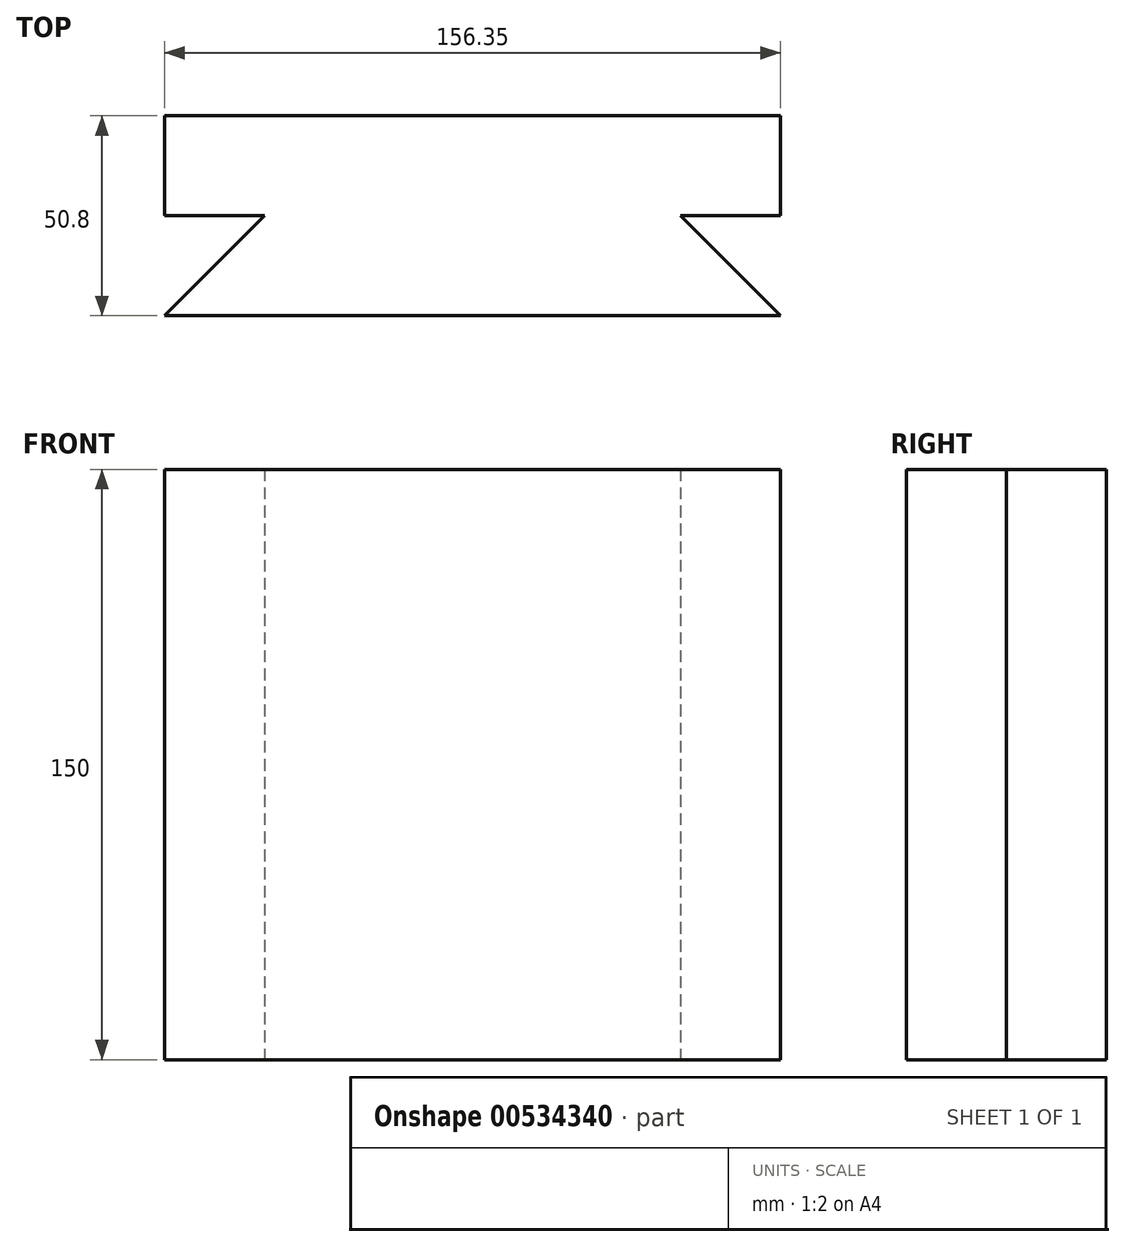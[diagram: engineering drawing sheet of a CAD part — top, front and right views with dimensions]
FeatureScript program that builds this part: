
annotation { "Feature Type Name" : "Feature", "Feature Type Description" : "" }
export const myFeature = defineFeature(function(context is Context, id is Id, definition is map)
    precondition{}
    {
        {
            var Q0;
            Q0=qCreatedBy(makeId("Top.planeOp"),FACE);
            var sketch = newSketch(context, id + "F0", { "sketchPlane" : qUnion([Q0])});
            skLineSegment(sketch, "E0.bottom", {"start": v(-77.43, 55.7) * mm, "end": v(78.92, 55.7) * mm});
            skLineSegment(sketch, "E0.top", {"start": v(-77.43, 30.3) * mm, "end": v(-52.03, 30.3) * mm});
            skLineSegment(sketch, "E0.left", {"start": v(-77.43, 55.7) * mm, "end": v(-77.43, 30.3) * mm});
            skLineSegment(sketch, "E0.right", {"start": v(78.92, 55.7) * mm, "end": v(78.92, 30.3) * mm});
            skLineSegment(sketch, "E1", {"start": v(-52.03, 30.3) * mm, "end": v(-52.03, 4.9) * mm, "construction": true});
            skLineSegment(sketch, "E2", {"start": v(53.52, 30.3) * mm, "end": v(53.52, 4.9) * mm, "construction": true});
            skLineSegment(sketch, "E3.trimOffspring", {"start": v(53.52, 30.3) * mm, "end": v(78.92, 30.3) * mm});
            skLineSegment(sketch, "E4", {"start": v(0, 55.7) * mm, "end": v(0, 4.9) * mm, "construction": true});
            skLineSegment(sketch, "E5", {"start": v(-77.43, 30.3) * mm, "end": v(-77.43, 4.9) * mm, "construction": true});
            skLineSegment(sketch, "E6", {"start": v(78.92, 30.3) * mm, "end": v(78.92, 4.9) * mm, "construction": true});
            skLineSegment(sketch, "E7", {"start": v(53.52, 30.3) * mm, "end": v(78.92, 4.9) * mm});
            skLineSegment(sketch, "E8", {"start": v(-52.03, 30.3) * mm, "end": v(-77.43, 4.9) * mm});
            skLineSegment(sketch, "E9", {"start": v(78.92, 4.9) * mm, "end": v(-77.43, 4.9) * mm});
            skSolve(sketch);
        }
        {
            var Q0;
            Q0=makeQuery(id+"F0.imprint","IMPRINT",FACE,{"disambiguationData":[TD([[makeQuery(id+"F0.imprint","IMPRINT",EDGE,{"derivedFrom":sQuery(id+"F0.wireOp",EDGE,"E0.bottom")}),-1.0]])]});
            extrude(context, id + "F1", {"entities" : qUnion([Q0]), "depth" : 150 * mm, "offsetDistance" : 25.4 * mm});
        }
    });
